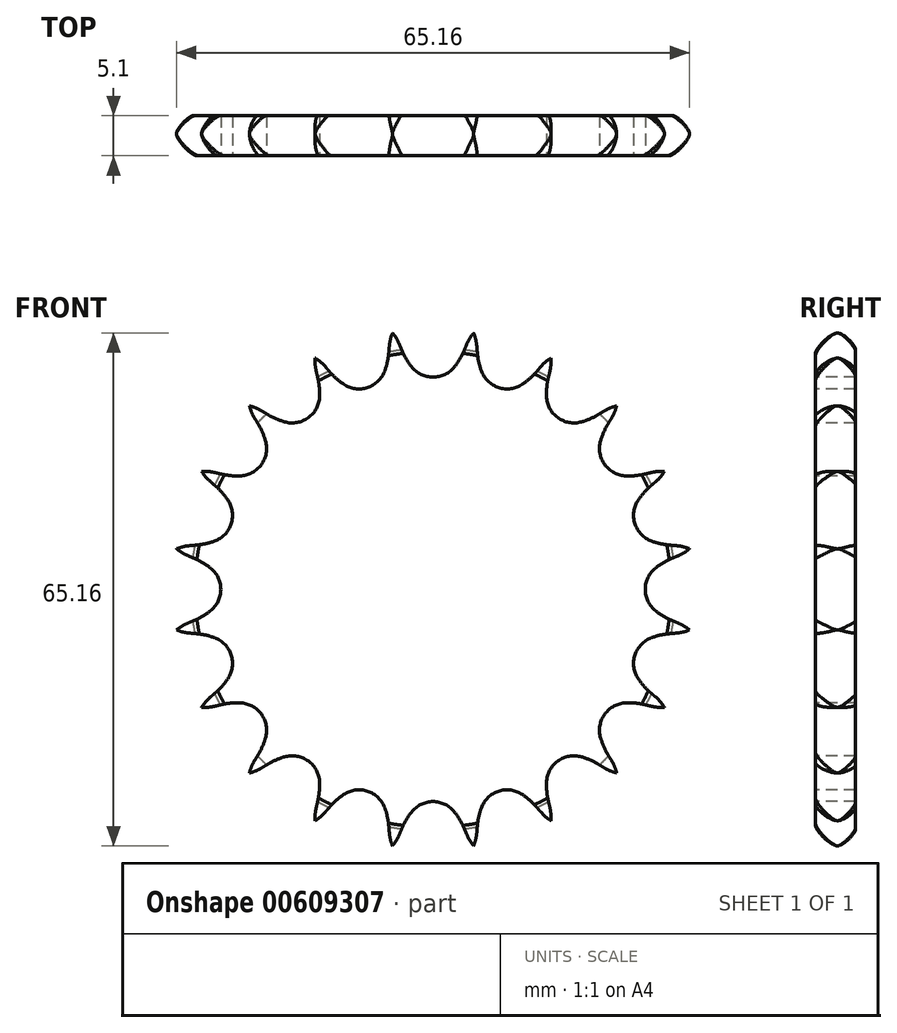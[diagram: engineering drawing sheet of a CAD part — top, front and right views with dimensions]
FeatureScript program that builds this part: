
annotation { "Feature Type Name" : "Feature", "Feature Type Description" : "" }
export const myFeature = defineFeature(function(context is Context, id is Id, definition is map)
    precondition{}
    {
        {
            var Q0;
            Q0=qCreatedBy(makeId("Right.planeOp"),FACE);
            var sketch = newSketch(context, id + "F0", { "sketchPlane" : qUnion([Q0])});
            skLineSegment(sketch, "E0", {"start": v(0, 0) * mm, "end": v(5.1, 0) * mm, "construction": true});
            skLineSegment(sketch, "E1", {"start": v(0, 32.98) * mm, "end": v(5.1, 32.98) * mm});
            skLineSegment(sketch, "E2", {"start": v(5.1, 32.98) * mm, "end": v(5.1, 30) * mm});
            skLineSegment(sketch, "E3", {"start": v(5.1, 30) * mm, "end": v(5.1, 30) * mm});
            skLineSegment(sketch, "E4", {"start": v(5.1, 30) * mm, "end": v(5.1, 0) * mm});
            skLineSegment(sketch, "E5", {"start": v(0, 0) * mm, "end": v(0, 32.98) * mm});
            skLineSegment(sketch, "E6.0.MirrorCS", {"start": v(0, -32.98) * mm, "end": v(5.1, -32.98) * mm});
            skLineSegment(sketch, "E6.1.MirrorCS", {"start": v(5.1, -32.98) * mm, "end": v(5.1, -30) * mm});
            skLineSegment(sketch, "E6.3.MirrorCS", {"start": v(5.1, -30) * mm, "end": v(5.1, 0) * mm});
            skLineSegment(sketch, "E6.4.MirrorCS", {"start": v(5.1, -30) * mm, "end": v(5.1, -30) * mm});
            skLineSegment(sketch, "E6.5.MirrorCS", {"start": v(0, 0) * mm, "end": v(0, -32.98) * mm});
            skLineSegment(sketch, "E7", {"start": v(0, 0) * mm, "end": v(5.1, 0) * mm});
            skLineSegment(sketch, "E8", {"start": v(5.1, 30) * mm, "end": v(0, 30) * mm, "construction": true});
            skLineSegment(sketch, "E9", {"start": v(5.1, -30) * mm, "end": v(0, -30) * mm, "construction": true});
            skSolve(sketch);
        }
        {
            var Q0;
            Q0=makeQuery(id+"F0.imprint","IMPRINT",FACE,{"disambiguationData":[TD([[makeQuery(id+"F0.imprint","IMPRINT",EDGE,{"derivedFrom":sQuery(id+"F0.wireOp",EDGE,"E1")}),-1.0]])]});
            var Q1;
            Q1=sQuery(id+"F0.wireOp",EDGE,"E0");
            revolve(context, id + "F1", {"entities" : qUnion([Q0]), "axis" : qUnion([Q1]), "revolveType" : RevolveType.FULL});
        }
        {
            var Q0;
            Q0=makeQuery(id+"F1.opRevolve","SWEPT_EDGE",EDGE,{"disambiguationData":[OSD([sQuery(id+"F0.wireOp",EDGE,"E1"),sQuery(id+"F0.wireOp",EDGE,"E5")])]});
            fillet(context, id + "F2", {"entities" : qUnion([Q0]), "radius" : 2.75 * mm, "tangentPropagation" : true, "rho" : 0.2, "crossSection" : FilletCrossSection.CONIC, "allowEdgeOverflow" : false});
        }
        {
            var Q0;
            Q0=makeQuery(id+"F1.opRevolve","SWEPT_EDGE",EDGE,{"disambiguationData":[OSD([sQuery(id+"F0.wireOp",EDGE,"E1"),sQuery(id+"F0.wireOp",EDGE,"E2")])]});
            fillet(context, id + "F3", {"entities" : qUnion([Q0]), "radius" : 2.25 * mm, "tangentPropagation" : true, "rho" : 0.2, "crossSection" : FilletCrossSection.CONIC, "allowEdgeOverflow" : false});
        }
        {
            var Q0;
            Q0=makeQuery(id+"F1.opRevolve","SWEPT_FACE",FACE,{"disambiguationData":[OSD([sQuery(id+"F0.wireOp",EDGE,"E5")])]});
            var sketch = newSketch(context, id + "F4", { "sketchPlane" : qUnion([Q0])});
            skCircle(sketch, "E10", {"center": v(0, 0) * mm, "radius": 30.44 * mm, "construction": true});
            skLineSegment(sketch, "E11", {"start": v(0, 0) * mm, "end": v(0, 30.44) * mm, "construction": true});
            skLineSegment(sketch, "E12", {"start": v(0, 30.44) * mm, "end": v(17.07, 30.44) * mm, "construction": true});
            skLineSegment(sketch, "E13", {"start": v(0, 30.44) * mm, "end": v(4.32, 33.82) * mm, "construction": true});
            skLineSegment(sketch, "E14", {"start": v(4.32, 33.82) * mm, "end": v(-3.95, 30.35) * mm, "construction": true});
            skLineSegment(sketch, "E15", {"start": v(-3.95, 30.35) * mm, "end": v(-4.28, 31.13) * mm});
            skLineSegment(sketch, "E16", {"start": v(0, 0) * mm, "end": v(-5.16, 32.58) * mm, "construction": true});
            skArc(sketch, "E17", {"start": v(-5.16, 32.58) * mm, "mid": v(-14.3, 26) * mm, "end": v(-4.28, 31.13) * mm, "construction": true});
            skArc(sketch, "E18", {"start": v(-4.28, 31.13) * mm, "mid": v(-4.66, 31.89) * mm, "end": v(-5.16, 32.58) * mm});
            skLineSegment(sketch, "E19", {"start": v(-4.28, 31.13) * mm, "end": v(-10.5, 45.96) * mm, "construction": true});
            skArc(sketch, "E20", {"start": v(-3.95, 30.35) * mm, "mid": v(-3.41, 29.28) * mm, "end": v(-2.75, 28.3) * mm});
            skArc(sketch, "E21", {"start": v(-2.75, 28.3) * mm, "mid": v(12.06, 38.36) * mm, "end": v(-3.95, 30.35) * mm, "construction": true});
            skArc(sketch, "E22.0.MirrorCS", {"start": v(3.95, 30.35) * mm, "mid": v(3.41, 29.28) * mm, "end": v(2.75, 28.3) * mm});
            skLineSegment(sketch, "E23.0.MirrorCS", {"start": v(3.95, 30.35) * mm, "end": v(4.28, 31.13) * mm});
            skArc(sketch, "E24.0.MirrorCS", {"start": v(4.28, 31.13) * mm, "mid": v(4.66, 31.89) * mm, "end": v(5.16, 32.58) * mm});
            skArc(sketch, "E25", {"start": v(-2.75, 28.3) * mm, "mid": v(0, 26.96) * mm, "end": v(2.75, 28.3) * mm});
            skArc(sketch, "E26", {"start": v(2.75, 28.3) * mm, "mid": v(0, 33.93) * mm, "end": v(-2.75, 28.3) * mm, "construction": true});
            skLineSegment(sketch, "E27", {"start": v(-49.44, 0) * mm, "end": v(0, 0) * mm, "construction": true});
            skArc(sketch, "E28.1.0", {"start": v(-5.55, 30.93) * mm, "mid": v(-5.42, 31.77) * mm, "end": v(-5.16, 32.58) * mm});
            skLineSegment(sketch, "E28.1.1", {"start": v(-5.62, 30.08) * mm, "end": v(-5.55, 30.93) * mm});
            skArc(sketch, "E28.1.2", {"start": v(-5.62, 30.08) * mm, "mid": v(-5.8, 28.9) * mm, "end": v(-6.13, 27.76) * mm});
            skArc(sketch, "E28.1.3", {"start": v(-11.36, 26.07) * mm, "mid": v(-8.33, 25.64) * mm, "end": v(-6.13, 27.76) * mm});
            skArc(sketch, "E28.1.4", {"start": v(-13.13, 27.64) * mm, "mid": v(-12.3, 26.8) * mm, "end": v(-11.36, 26.07) * mm});
            skLineSegment(sketch, "E28.1.5", {"start": v(-13.13, 27.64) * mm, "end": v(-13.69, 28.29) * mm});
            skArc(sketch, "E28.1.6", {"start": v(-13.69, 28.29) * mm, "mid": v(-14.29, 28.89) * mm, "end": v(-14.97, 29.39) * mm});
            skArc(sketch, "E28.2.0", {"start": v(-14.84, 27.7) * mm, "mid": v(-14.97, 28.54) * mm, "end": v(-14.97, 29.39) * mm});
            skLineSegment(sketch, "E28.2.1", {"start": v(-14.64, 26.87) * mm, "end": v(-14.84, 27.7) * mm});
            skArc(sketch, "E28.2.2", {"start": v(-14.64, 26.87) * mm, "mid": v(-14.45, 25.7) * mm, "end": v(-14.41, 24.5) * mm});
            skArc(sketch, "E28.2.3", {"start": v(-18.85, 21.28) * mm, "mid": v(-15.85, 21.81) * mm, "end": v(-14.41, 24.5) * mm});
            skArc(sketch, "E28.2.4", {"start": v(-21.03, 22.23) * mm, "mid": v(-19.97, 21.68) * mm, "end": v(-18.85, 21.28) * mm});
            skLineSegment(sketch, "E28.2.5", {"start": v(-21.03, 22.23) * mm, "end": v(-21.76, 22.67) * mm});
            skArc(sketch, "E28.2.6", {"start": v(-21.76, 22.67) * mm, "mid": v(-22.52, 23.06) * mm, "end": v(-23.32, 23.32) * mm});
            skArc(sketch, "E28.3.0", {"start": v(-22.67, 21.76) * mm, "mid": v(-23.06, 22.52) * mm, "end": v(-23.32, 23.32) * mm});
            skLineSegment(sketch, "E28.3.1", {"start": v(-22.23, 21.03) * mm, "end": v(-22.67, 21.76) * mm});
            skArc(sketch, "E28.3.2", {"start": v(-22.23, 21.03) * mm, "mid": v(-21.68, 19.97) * mm, "end": v(-21.28, 18.85) * mm});
            skArc(sketch, "E28.3.3", {"start": v(-24.5, 14.41) * mm, "mid": v(-21.81, 15.85) * mm, "end": v(-21.28, 18.85) * mm});
            skArc(sketch, "E28.3.4", {"start": v(-26.87, 14.64) * mm, "mid": v(-25.7, 14.45) * mm, "end": v(-24.5, 14.41) * mm});
            skLineSegment(sketch, "E28.3.5", {"start": v(-26.87, 14.64) * mm, "end": v(-27.7, 14.84) * mm});
            skArc(sketch, "E28.3.6", {"start": v(-27.7, 14.84) * mm, "mid": v(-28.54, 14.97) * mm, "end": v(-29.39, 14.97) * mm});
            skArc(sketch, "E28.4.0", {"start": v(-28.29, 13.69) * mm, "mid": v(-28.89, 14.29) * mm, "end": v(-29.39, 14.97) * mm});
            skLineSegment(sketch, "E28.4.1", {"start": v(-27.64, 13.13) * mm, "end": v(-28.29, 13.69) * mm});
            skArc(sketch, "E28.4.2", {"start": v(-27.64, 13.13) * mm, "mid": v(-26.8, 12.3) * mm, "end": v(-26.07, 11.36) * mm});
            skArc(sketch, "E28.4.3", {"start": v(-27.76, 6.13) * mm, "mid": v(-25.64, 8.33) * mm, "end": v(-26.07, 11.36) * mm});
            skArc(sketch, "E28.4.4", {"start": v(-30.08, 5.62) * mm, "mid": v(-28.9, 5.8) * mm, "end": v(-27.76, 6.13) * mm});
            skLineSegment(sketch, "E28.4.5", {"start": v(-30.08, 5.62) * mm, "end": v(-30.93, 5.55) * mm});
            skArc(sketch, "E28.4.6", {"start": v(-30.93, 5.55) * mm, "mid": v(-31.77, 5.42) * mm, "end": v(-32.58, 5.16) * mm});
            skArc(sketch, "E28.5.0", {"start": v(-31.13, 4.28) * mm, "mid": v(-31.89, 4.66) * mm, "end": v(-32.58, 5.16) * mm});
            skLineSegment(sketch, "E28.5.1", {"start": v(-30.35, 3.95) * mm, "end": v(-31.13, 4.28) * mm});
            skArc(sketch, "E28.5.2", {"start": v(-30.35, 3.95) * mm, "mid": v(-29.28, 3.41) * mm, "end": v(-28.3, 2.75) * mm});
            skArc(sketch, "E28.5.3", {"start": v(-28.3, -2.75) * mm, "mid": v(-26.96, 0) * mm, "end": v(-28.3, 2.75) * mm});
            skArc(sketch, "E28.5.4", {"start": v(-30.35, -3.95) * mm, "mid": v(-29.28, -3.41) * mm, "end": v(-28.3, -2.75) * mm});
            skLineSegment(sketch, "E28.5.5", {"start": v(-30.35, -3.95) * mm, "end": v(-31.13, -4.28) * mm});
            skArc(sketch, "E28.5.6", {"start": v(-31.13, -4.28) * mm, "mid": v(-31.89, -4.66) * mm, "end": v(-32.58, -5.16) * mm});
            skArc(sketch, "E28.6.0", {"start": v(-30.93, -5.55) * mm, "mid": v(-31.77, -5.42) * mm, "end": v(-32.58, -5.16) * mm});
            skLineSegment(sketch, "E28.6.1", {"start": v(-30.08, -5.62) * mm, "end": v(-30.93, -5.55) * mm});
            skArc(sketch, "E28.6.2", {"start": v(-30.08, -5.62) * mm, "mid": v(-28.9, -5.8) * mm, "end": v(-27.76, -6.13) * mm});
            skArc(sketch, "E28.6.3", {"start": v(-26.07, -11.36) * mm, "mid": v(-25.64, -8.33) * mm, "end": v(-27.76, -6.13) * mm});
            skArc(sketch, "E28.6.4", {"start": v(-27.64, -13.13) * mm, "mid": v(-26.8, -12.3) * mm, "end": v(-26.07, -11.36) * mm});
            skLineSegment(sketch, "E28.6.5", {"start": v(-27.64, -13.13) * mm, "end": v(-28.29, -13.69) * mm});
            skArc(sketch, "E28.6.6", {"start": v(-28.29, -13.69) * mm, "mid": v(-28.89, -14.29) * mm, "end": v(-29.39, -14.97) * mm});
            skArc(sketch, "E28.7.0", {"start": v(-27.7, -14.84) * mm, "mid": v(-28.54, -14.97) * mm, "end": v(-29.39, -14.97) * mm});
            skLineSegment(sketch, "E28.7.1", {"start": v(-26.87, -14.64) * mm, "end": v(-27.7, -14.84) * mm});
            skArc(sketch, "E28.7.2", {"start": v(-26.87, -14.64) * mm, "mid": v(-25.7, -14.45) * mm, "end": v(-24.5, -14.41) * mm});
            skArc(sketch, "E28.7.3", {"start": v(-21.28, -18.85) * mm, "mid": v(-21.81, -15.85) * mm, "end": v(-24.5, -14.41) * mm});
            skArc(sketch, "E28.7.4", {"start": v(-22.23, -21.03) * mm, "mid": v(-21.68, -19.97) * mm, "end": v(-21.28, -18.85) * mm});
            skLineSegment(sketch, "E28.7.5", {"start": v(-22.23, -21.03) * mm, "end": v(-22.67, -21.76) * mm});
            skArc(sketch, "E28.7.6", {"start": v(-22.67, -21.76) * mm, "mid": v(-23.06, -22.52) * mm, "end": v(-23.32, -23.32) * mm});
            skArc(sketch, "E28.8.0", {"start": v(-21.76, -22.67) * mm, "mid": v(-22.52, -23.06) * mm, "end": v(-23.32, -23.32) * mm});
            skLineSegment(sketch, "E28.8.1", {"start": v(-21.03, -22.23) * mm, "end": v(-21.76, -22.67) * mm});
            skArc(sketch, "E28.8.2", {"start": v(-21.03, -22.23) * mm, "mid": v(-19.97, -21.68) * mm, "end": v(-18.85, -21.28) * mm});
            skArc(sketch, "E28.8.3", {"start": v(-14.41, -24.5) * mm, "mid": v(-15.85, -21.81) * mm, "end": v(-18.85, -21.28) * mm});
            skArc(sketch, "E28.8.4", {"start": v(-14.64, -26.87) * mm, "mid": v(-14.45, -25.7) * mm, "end": v(-14.41, -24.5) * mm});
            skLineSegment(sketch, "E28.8.5", {"start": v(-14.64, -26.87) * mm, "end": v(-14.84, -27.7) * mm});
            skArc(sketch, "E28.8.6", {"start": v(-14.84, -27.7) * mm, "mid": v(-14.97, -28.54) * mm, "end": v(-14.97, -29.39) * mm});
            skArc(sketch, "E28.9.0", {"start": v(-13.69, -28.29) * mm, "mid": v(-14.29, -28.89) * mm, "end": v(-14.97, -29.39) * mm});
            skLineSegment(sketch, "E28.9.1", {"start": v(-13.13, -27.64) * mm, "end": v(-13.69, -28.29) * mm});
            skArc(sketch, "E28.9.2", {"start": v(-13.13, -27.64) * mm, "mid": v(-12.3, -26.8) * mm, "end": v(-11.36, -26.07) * mm});
            skArc(sketch, "E28.9.3", {"start": v(-6.13, -27.76) * mm, "mid": v(-8.33, -25.64) * mm, "end": v(-11.36, -26.07) * mm});
            skArc(sketch, "E28.9.4", {"start": v(-5.62, -30.08) * mm, "mid": v(-5.8, -28.9) * mm, "end": v(-6.13, -27.76) * mm});
            skLineSegment(sketch, "E28.9.5", {"start": v(-5.62, -30.08) * mm, "end": v(-5.55, -30.93) * mm});
            skArc(sketch, "E28.9.6", {"start": v(-5.55, -30.93) * mm, "mid": v(-5.42, -31.77) * mm, "end": v(-5.16, -32.58) * mm});
            skArc(sketch, "E28.10.0", {"start": v(-4.28, -31.13) * mm, "mid": v(-4.66, -31.89) * mm, "end": v(-5.16, -32.58) * mm});
            skLineSegment(sketch, "E28.10.1", {"start": v(-3.95, -30.35) * mm, "end": v(-4.28, -31.13) * mm});
            skArc(sketch, "E28.10.2", {"start": v(-3.95, -30.35) * mm, "mid": v(-3.41, -29.28) * mm, "end": v(-2.75, -28.3) * mm});
            skArc(sketch, "E28.10.3", {"start": v(2.75, -28.3) * mm, "mid": v(0, -26.96) * mm, "end": v(-2.75, -28.3) * mm});
            skArc(sketch, "E28.10.4", {"start": v(3.95, -30.35) * mm, "mid": v(3.41, -29.28) * mm, "end": v(2.75, -28.3) * mm});
            skLineSegment(sketch, "E28.10.5", {"start": v(3.95, -30.35) * mm, "end": v(4.28, -31.13) * mm});
            skArc(sketch, "E28.10.6", {"start": v(4.28, -31.13) * mm, "mid": v(4.66, -31.89) * mm, "end": v(5.16, -32.58) * mm});
            skArc(sketch, "E28.11.0", {"start": v(5.55, -30.93) * mm, "mid": v(5.42, -31.77) * mm, "end": v(5.16, -32.58) * mm});
            skLineSegment(sketch, "E28.11.1", {"start": v(5.62, -30.08) * mm, "end": v(5.55, -30.93) * mm});
            skArc(sketch, "E28.11.2", {"start": v(5.62, -30.08) * mm, "mid": v(5.8, -28.9) * mm, "end": v(6.13, -27.76) * mm});
            skArc(sketch, "E28.11.3", {"start": v(11.36, -26.07) * mm, "mid": v(8.33, -25.64) * mm, "end": v(6.13, -27.76) * mm});
            skArc(sketch, "E28.11.4", {"start": v(13.13, -27.64) * mm, "mid": v(12.3, -26.8) * mm, "end": v(11.36, -26.07) * mm});
            skLineSegment(sketch, "E28.11.5", {"start": v(13.13, -27.64) * mm, "end": v(13.69, -28.29) * mm});
            skArc(sketch, "E28.11.6", {"start": v(13.69, -28.29) * mm, "mid": v(14.29, -28.89) * mm, "end": v(14.97, -29.39) * mm});
            skArc(sketch, "E28.12.0", {"start": v(14.84, -27.7) * mm, "mid": v(14.97, -28.54) * mm, "end": v(14.97, -29.39) * mm});
            skLineSegment(sketch, "E28.12.1", {"start": v(14.64, -26.87) * mm, "end": v(14.84, -27.7) * mm});
            skArc(sketch, "E28.12.2", {"start": v(14.64, -26.87) * mm, "mid": v(14.45, -25.7) * mm, "end": v(14.41, -24.5) * mm});
            skArc(sketch, "E28.12.3", {"start": v(18.85, -21.28) * mm, "mid": v(15.85, -21.81) * mm, "end": v(14.41, -24.5) * mm});
            skArc(sketch, "E28.12.4", {"start": v(21.03, -22.23) * mm, "mid": v(19.97, -21.68) * mm, "end": v(18.85, -21.28) * mm});
            skLineSegment(sketch, "E28.12.5", {"start": v(21.03, -22.23) * mm, "end": v(21.76, -22.67) * mm});
            skArc(sketch, "E28.12.6", {"start": v(21.76, -22.67) * mm, "mid": v(22.52, -23.06) * mm, "end": v(23.32, -23.32) * mm});
            skArc(sketch, "E28.13.0", {"start": v(22.67, -21.76) * mm, "mid": v(23.06, -22.52) * mm, "end": v(23.32, -23.32) * mm});
            skLineSegment(sketch, "E28.13.1", {"start": v(22.23, -21.03) * mm, "end": v(22.67, -21.76) * mm});
            skArc(sketch, "E28.13.2", {"start": v(22.23, -21.03) * mm, "mid": v(21.68, -19.97) * mm, "end": v(21.28, -18.85) * mm});
            skArc(sketch, "E28.13.3", {"start": v(24.5, -14.41) * mm, "mid": v(21.81, -15.85) * mm, "end": v(21.28, -18.85) * mm});
            skArc(sketch, "E28.13.4", {"start": v(26.87, -14.64) * mm, "mid": v(25.7, -14.45) * mm, "end": v(24.5, -14.41) * mm});
            skLineSegment(sketch, "E28.13.5", {"start": v(26.87, -14.64) * mm, "end": v(27.7, -14.84) * mm});
            skArc(sketch, "E28.13.6", {"start": v(27.7, -14.84) * mm, "mid": v(28.54, -14.97) * mm, "end": v(29.39, -14.97) * mm});
            skArc(sketch, "E28.14.0", {"start": v(28.29, -13.69) * mm, "mid": v(28.89, -14.29) * mm, "end": v(29.39, -14.97) * mm});
            skLineSegment(sketch, "E28.14.1", {"start": v(27.64, -13.13) * mm, "end": v(28.29, -13.69) * mm});
            skArc(sketch, "E28.14.2", {"start": v(27.64, -13.13) * mm, "mid": v(26.8, -12.3) * mm, "end": v(26.07, -11.36) * mm});
            skArc(sketch, "E28.14.3", {"start": v(27.76, -6.13) * mm, "mid": v(25.64, -8.33) * mm, "end": v(26.07, -11.36) * mm});
            skArc(sketch, "E28.14.4", {"start": v(30.08, -5.62) * mm, "mid": v(28.9, -5.8) * mm, "end": v(27.76, -6.13) * mm});
            skLineSegment(sketch, "E28.14.5", {"start": v(30.08, -5.62) * mm, "end": v(30.93, -5.55) * mm});
            skArc(sketch, "E28.14.6", {"start": v(30.93, -5.55) * mm, "mid": v(31.77, -5.42) * mm, "end": v(32.58, -5.16) * mm});
            skArc(sketch, "E28.15.0", {"start": v(31.13, -4.28) * mm, "mid": v(31.89, -4.66) * mm, "end": v(32.58, -5.16) * mm});
            skLineSegment(sketch, "E28.15.1", {"start": v(30.35, -3.95) * mm, "end": v(31.13, -4.28) * mm});
            skArc(sketch, "E28.15.2", {"start": v(30.35, -3.95) * mm, "mid": v(29.28, -3.41) * mm, "end": v(28.3, -2.75) * mm});
            skArc(sketch, "E28.15.3", {"start": v(28.3, 2.75) * mm, "mid": v(26.96, 0) * mm, "end": v(28.3, -2.75) * mm});
            skArc(sketch, "E28.15.4", {"start": v(30.35, 3.95) * mm, "mid": v(29.28, 3.41) * mm, "end": v(28.3, 2.75) * mm});
            skLineSegment(sketch, "E28.15.5", {"start": v(30.35, 3.95) * mm, "end": v(31.13, 4.28) * mm});
            skArc(sketch, "E28.15.6", {"start": v(31.13, 4.28) * mm, "mid": v(31.89, 4.66) * mm, "end": v(32.58, 5.16) * mm});
            skArc(sketch, "E28.16.0", {"start": v(30.93, 5.55) * mm, "mid": v(31.77, 5.42) * mm, "end": v(32.58, 5.16) * mm});
            skLineSegment(sketch, "E28.16.1", {"start": v(30.08, 5.62) * mm, "end": v(30.93, 5.55) * mm});
            skArc(sketch, "E28.16.2", {"start": v(30.08, 5.62) * mm, "mid": v(28.9, 5.8) * mm, "end": v(27.76, 6.13) * mm});
            skArc(sketch, "E28.16.3", {"start": v(26.07, 11.36) * mm, "mid": v(25.64, 8.33) * mm, "end": v(27.76, 6.13) * mm});
            skArc(sketch, "E28.16.4", {"start": v(27.64, 13.13) * mm, "mid": v(26.8, 12.3) * mm, "end": v(26.07, 11.36) * mm});
            skLineSegment(sketch, "E28.16.5", {"start": v(27.64, 13.13) * mm, "end": v(28.29, 13.69) * mm});
            skArc(sketch, "E28.16.6", {"start": v(28.29, 13.69) * mm, "mid": v(28.89, 14.29) * mm, "end": v(29.39, 14.97) * mm});
            skArc(sketch, "E28.17.0", {"start": v(27.7, 14.84) * mm, "mid": v(28.54, 14.97) * mm, "end": v(29.39, 14.97) * mm});
            skLineSegment(sketch, "E28.17.1", {"start": v(26.87, 14.64) * mm, "end": v(27.7, 14.84) * mm});
            skArc(sketch, "E28.17.2", {"start": v(26.87, 14.64) * mm, "mid": v(25.7, 14.45) * mm, "end": v(24.5, 14.41) * mm});
            skArc(sketch, "E28.17.3", {"start": v(21.28, 18.85) * mm, "mid": v(21.81, 15.85) * mm, "end": v(24.5, 14.41) * mm});
            skArc(sketch, "E28.17.4", {"start": v(22.23, 21.03) * mm, "mid": v(21.68, 19.97) * mm, "end": v(21.28, 18.85) * mm});
            skLineSegment(sketch, "E28.17.5", {"start": v(22.23, 21.03) * mm, "end": v(22.67, 21.76) * mm});
            skArc(sketch, "E28.17.6", {"start": v(22.67, 21.76) * mm, "mid": v(23.06, 22.52) * mm, "end": v(23.32, 23.32) * mm});
            skArc(sketch, "E28.18.0", {"start": v(21.76, 22.67) * mm, "mid": v(22.52, 23.06) * mm, "end": v(23.32, 23.32) * mm});
            skLineSegment(sketch, "E28.18.1", {"start": v(21.03, 22.23) * mm, "end": v(21.76, 22.67) * mm});
            skArc(sketch, "E28.18.2", {"start": v(21.03, 22.23) * mm, "mid": v(19.97, 21.68) * mm, "end": v(18.85, 21.28) * mm});
            skArc(sketch, "E28.18.3", {"start": v(14.41, 24.5) * mm, "mid": v(15.85, 21.81) * mm, "end": v(18.85, 21.28) * mm});
            skArc(sketch, "E28.18.4", {"start": v(14.64, 26.87) * mm, "mid": v(14.45, 25.7) * mm, "end": v(14.41, 24.5) * mm});
            skLineSegment(sketch, "E28.18.5", {"start": v(14.64, 26.87) * mm, "end": v(14.84, 27.7) * mm});
            skArc(sketch, "E28.18.6", {"start": v(14.84, 27.7) * mm, "mid": v(14.97, 28.54) * mm, "end": v(14.97, 29.39) * mm});
            skArc(sketch, "E28.19.0", {"start": v(13.69, 28.29) * mm, "mid": v(14.29, 28.89) * mm, "end": v(14.97, 29.39) * mm});
            skLineSegment(sketch, "E28.19.1", {"start": v(13.13, 27.64) * mm, "end": v(13.69, 28.29) * mm});
            skArc(sketch, "E28.19.2", {"start": v(13.13, 27.64) * mm, "mid": v(12.3, 26.8) * mm, "end": v(11.36, 26.07) * mm});
            skArc(sketch, "E28.19.3", {"start": v(6.13, 27.76) * mm, "mid": v(8.33, 25.64) * mm, "end": v(11.36, 26.07) * mm});
            skArc(sketch, "E28.19.4", {"start": v(5.62, 30.08) * mm, "mid": v(5.8, 28.9) * mm, "end": v(6.13, 27.76) * mm});
            skLineSegment(sketch, "E28.19.5", {"start": v(5.62, 30.08) * mm, "end": v(5.55, 30.93) * mm});
            skArc(sketch, "E28.19.6", {"start": v(5.55, 30.93) * mm, "mid": v(5.42, 31.77) * mm, "end": v(5.16, 32.58) * mm});
            skSolve(sketch);
        }
        {
            var Q0;
            Q0=qSketchRegion(id+"F4",true);
            extrude(context, id + "F5", {"entities" : qUnion([Q0]), "operationType" : NewBodyOperationType.INTERSECT, "endBound" : BoundingType.THROUGH_ALL, "oppositeDirection" : true, "depth" : 25.4 * mm});
        }
    });
